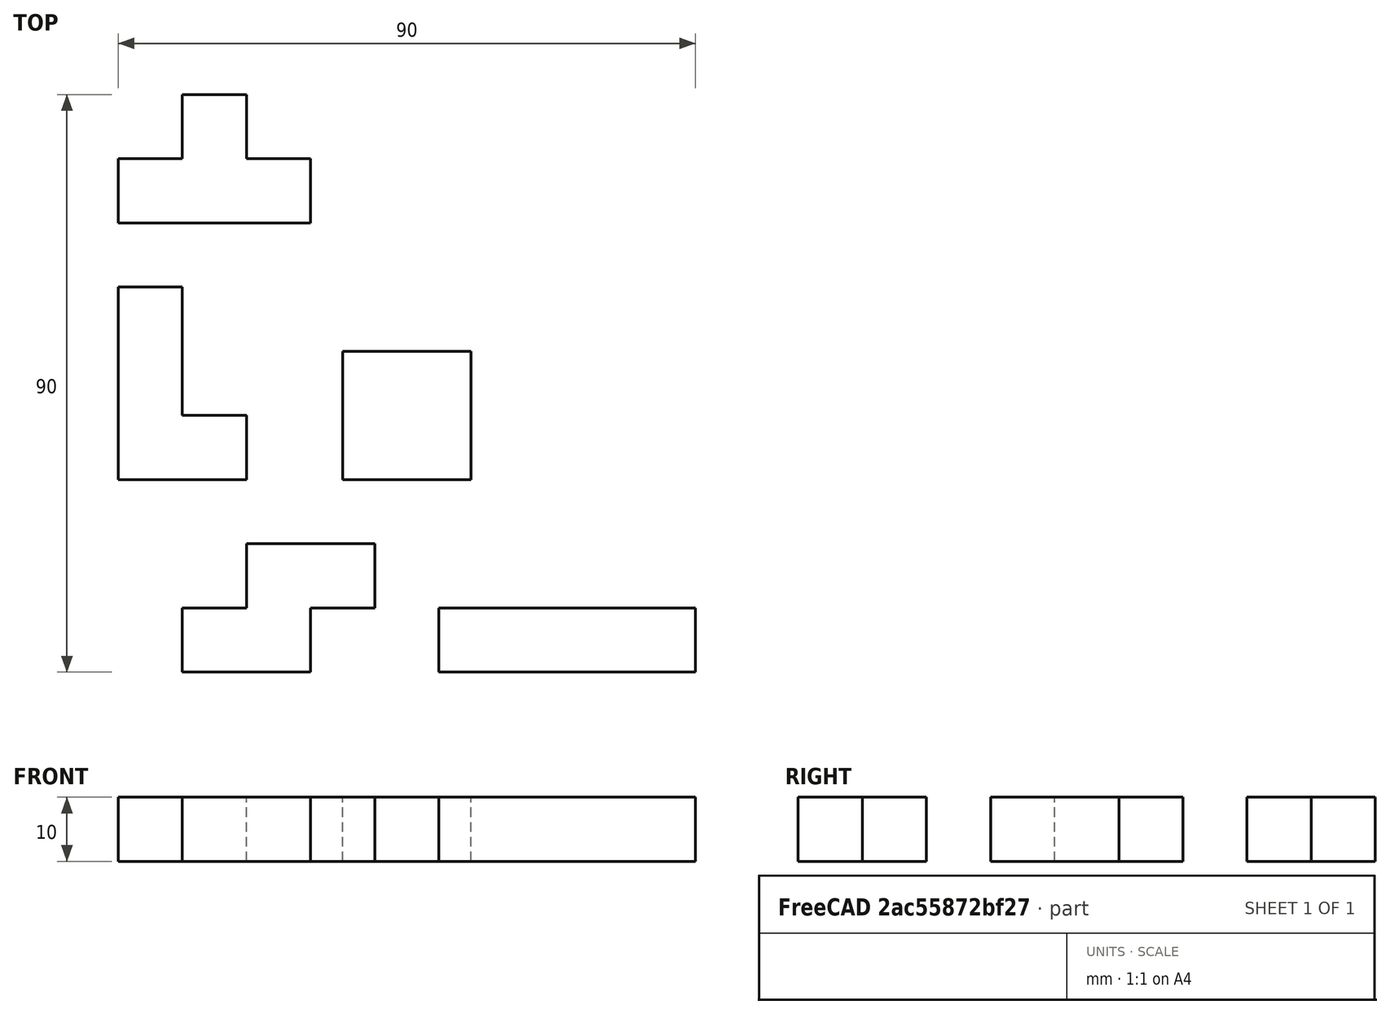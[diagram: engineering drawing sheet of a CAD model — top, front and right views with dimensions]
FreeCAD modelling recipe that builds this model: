
FCSTD DOCUMENT  (FreeCAD 0.21R33694 (Git))
Label: OJT1_T05R04_tetris
License: All rights reserved
LicenseURL: http://en.wikipedia.org/wiki/All_rights_reserved
objects: Part::Box×20, Part::MultiFuse×5
note: 25 computed .brp shape members not serialized (recipe doc carries the construction recipe); baked Part::Feature solids carry a one-line shape summary decoded from their .brp

FEATURE [Part::Box] Box  label="cubo1"
  AttacherType = Attacher::AttachEngine3D
  Height = 10
  Length = 10
  Width = 10
FEATURE [Part::Box] Box001  label="cubo2"
  AttacherType = Attacher::AttachEngine3D
  Height = 10
  Length = 10
  Placement = pos=(10,0,0) rot=(0,0,1;0rad)
  Width = 10
FEATURE [Part::Box] Box002  label="cubo3"
  AttacherType = Attacher::AttachEngine3D
  Height = 10
  Length = 10
  Placement = pos=(20,0,0) rot=(0,0,1;0rad)
  Width = 10
FEATURE [Part::Box] Box003  label="cubo4"
  AttacherType = Attacher::AttachEngine3D
  Height = 10
  Length = 10
  Placement = pos=(30,0,0) rot=(0,0,1;0rad)
  Width = 10
FEATURE [Part::MultiFuse] Fusion  label="Fusion1"
  Placement = pos=(50,0,0) rot=(0,0,1;0rad)
  Refine = true
  Shapes = -> [Box,Box001,Box002,Box003]
FEATURE [Part::Box] Box004  label="cubo5"
  AttacherType = Attacher::AttachEngine3D
  Height = 10
  Length = 10
  Width = 10
FEATURE [Part::Box] Box005  label="cubo6"
  AttacherType = Attacher::AttachEngine3D
  Height = 10
  Length = 10
  Placement = pos=(10,0,0) rot=(0,0,1;0rad)
  Width = 10
FEATURE [Part::Box] Box006  label="cubo7"
  AttacherType = Attacher::AttachEngine3D
  Height = 10
  Length = 10
  Placement = pos=(10,10,0) rot=(0,0,1;0rad)
  Width = 10
FEATURE [Part::Box] Box007  label="cubo8"
  AttacherType = Attacher::AttachEngine3D
  Height = 10
  Length = 10
  Placement = pos=(20,0,0) rot=(0,0,1;0rad)
  Width = 10
FEATURE [Part::MultiFuse] Fusion001  label="Fusion2"
  Placement = pos=(0,70,0) rot=(0,0,1;0rad)
  Refine = true
  Shapes = -> [Box004,Box005,Box006,Box007]
FEATURE [Part::Box] Box008  label="cubo9"
  AttacherType = Attacher::AttachEngine3D
  Height = 10
  Length = 10
  Width = 10
FEATURE [Part::Box] Box009  label="cubo10"
  AttacherType = Attacher::AttachEngine3D
  Height = 10
  Length = 10
  Placement = pos=(10,0,0) rot=(0,0,1;0rad)
  Width = 10
FEATURE [Part::Box] Box010  label="cubo11"
  AttacherType = Attacher::AttachEngine3D
  Height = 10
  Length = 10
  Placement = pos=(10,10,0) rot=(0,0,1;0rad)
  Width = 10
FEATURE [Part::Box] Box011  label="cubo12"
  AttacherType = Attacher::AttachEngine3D
  Height = 10
  Length = 10
  Placement = pos=(0,10,0) rot=(0,0,1;0rad)
  Width = 10
FEATURE [Part::MultiFuse] Fusion002  label="Fusion3"
  Placement = pos=(35,30,0) rot=(0,0,1;0rad)
  Refine = true
  Shapes = -> [Box008,Box009,Box010,Box011]
FEATURE [Part::Box] Box012  label="cubo13"
  AttacherType = Attacher::AttachEngine3D
  Height = 10
  Length = 10
  Placement = pos=(10,0,0) rot=(0,0,1;0rad)
  Width = 10
FEATURE [Part::Box] Box013  label="cubo14"
  AttacherType = Attacher::AttachEngine3D
  Height = 10
  Length = 10
  Placement = pos=(0,10,0) rot=(0,0,1;0rad)
  Width = 10
FEATURE [Part::Box] Box014  label="cubo15"
  AttacherType = Attacher::AttachEngine3D
  Height = 10
  Length = 10
  Placement = pos=(0,20,0) rot=(0,0,1;0rad)
  Width = 10
FEATURE [Part::Box] Box015  label="cubo16"
  AttacherType = Attacher::AttachEngine3D
  Height = 10
  Length = 10
  Width = 10
FEATURE [Part::MultiFuse] Fusion003  label="Fusion4"
  Placement = pos=(0,30,0) rot=(0,0,1;0rad)
  Refine = true
  Shapes = -> [Box012,Box013,Box014,Box015]
FEATURE [Part::Box] Box016  label="cubo17"
  AttacherType = Attacher::AttachEngine3D
  Height = 10
  Length = 10
  Width = 10
FEATURE [Part::Box] Box017  label="cubo18"
  AttacherType = Attacher::AttachEngine3D
  Height = 10
  Length = 10
  Placement = pos=(10,0,0) rot=(0,0,1;0rad)
  Width = 10
FEATURE [Part::Box] Box018  label="cubo19"
  AttacherType = Attacher::AttachEngine3D
  Height = 10
  Length = 10
  Placement = pos=(10,10,0) rot=(0,0,1;0rad)
  Width = 10
FEATURE [Part::Box] Box019  label="cubo20"
  AttacherType = Attacher::AttachEngine3D
  Height = 10
  Length = 10
  Placement = pos=(20,10,0) rot=(0,0,1;0rad)
  Width = 10
FEATURE [Part::MultiFuse] Fusion004  label="Fusion5"
  Placement = pos=(10,0,0) rot=(0,0,1;0rad)
  Refine = true
  Shapes = -> [Box016,Box017,Box018,Box019]
